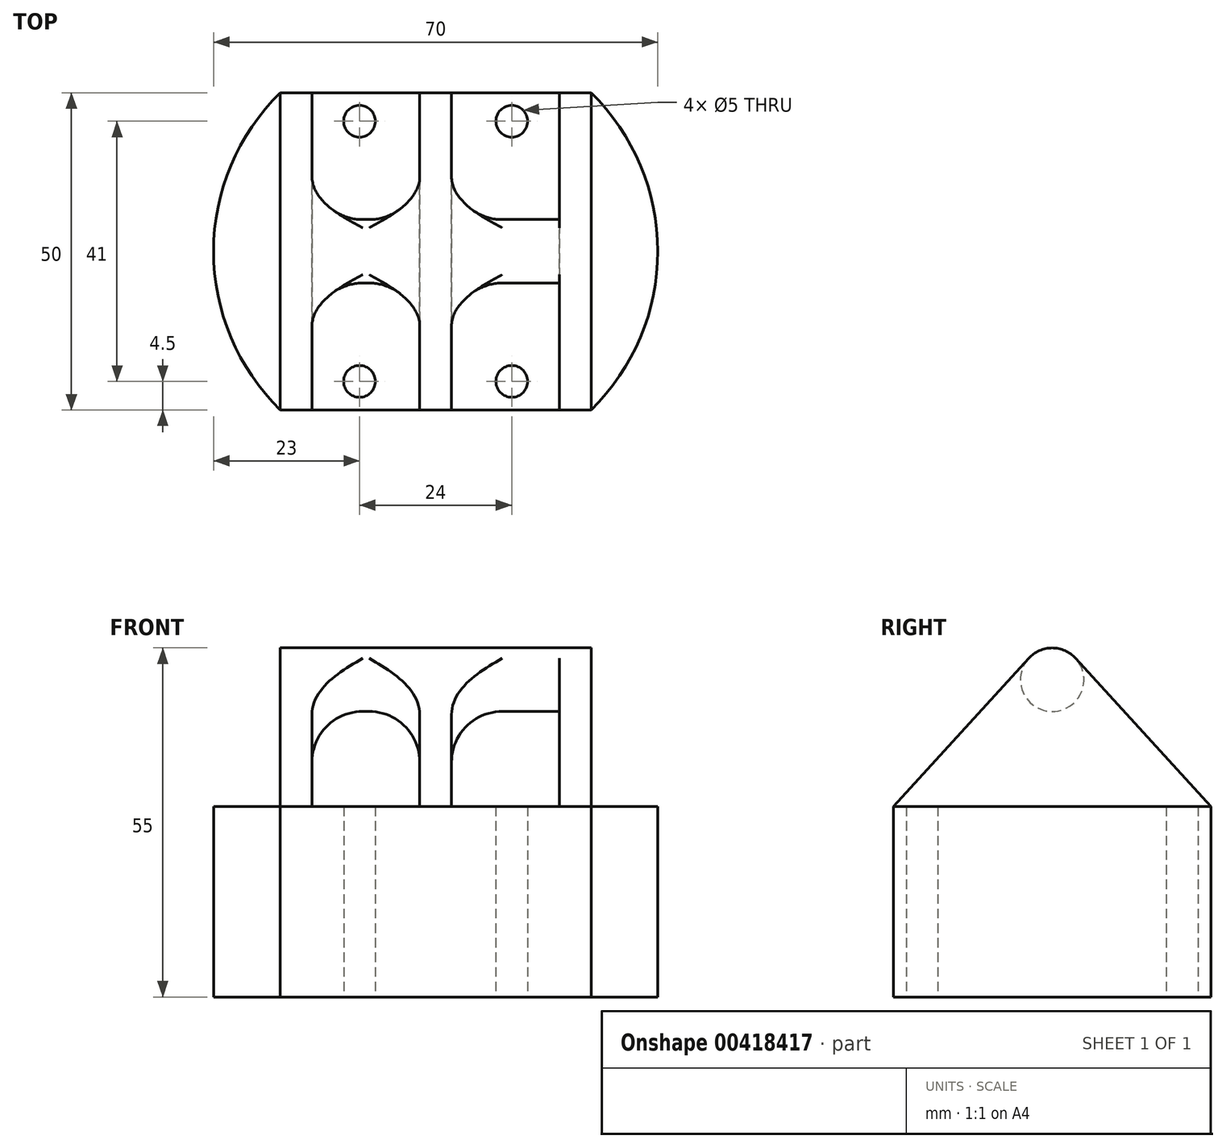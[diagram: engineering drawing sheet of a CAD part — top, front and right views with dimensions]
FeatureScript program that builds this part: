
annotation { "Feature Type Name" : "Feature", "Feature Type Description" : "" }
export const myFeature = defineFeature(function(context is Context, id is Id, definition is map)
    precondition{}
    {
        {
            var Q0;
            Q0=qCreatedBy(makeId("Top.planeOp"),FACE);
            var sketch = newSketch(context, id + "F0", { "sketchPlane" : qUnion([Q0])});
            skArc(sketch, "E0", {"start": v(-24.5, 25) * mm, "mid": v(-35, 0) * mm, "end": v(-24.5, -25) * mm});
            skLineSegment(sketch, "E1", {"start": v(-24.5, 25) * mm, "end": v(24.5, 25) * mm});
            skLineSegment(sketch, "E2", {"start": v(-24.5, -25) * mm, "end": v(24.5, -25) * mm});
            skArc(sketch, "E3.trimOffspring", {"start": v(24.5, -25) * mm, "mid": v(35, 0) * mm, "end": v(24.5, 25) * mm});
            skCircle(sketch, "E4", {"center": v(-12, -20.5) * mm, "radius": 2.5 * mm});
            skCircle(sketch, "E5", {"center": v(12, -20.5) * mm, "radius": 2.5 * mm});
            skCircle(sketch, "E6", {"center": v(12, 20.5) * mm, "radius": 2.5 * mm});
            skCircle(sketch, "E7", {"center": v(-12, 20.5) * mm, "radius": 2.5 * mm});
            skSolve(sketch);
        }
        {
            var Q0;
            Q0=qSketchRegion(id+"F0",true);
            extrude(context, id + "F1", {"entities" : qUnion([Q0]), "depth" : 5 * mm, "hasSecondDirection" : true, "secondDirectionOppositeDirection" : true, "secondDirectionDepth" : 25 * mm});
        }
        {
            var Q0;
            Q0=makeQuery(id+"F1.opExtrude","CAP_FACE",FACE,{"disambiguationData":[OSD([sQuery(id+"F0.wireOp",EDGE,"E0"),sQuery(id+"F0.wireOp",EDGE,"E1"),sQuery(id+"F0.wireOp",EDGE,"E2"),sQuery(id+"F0.wireOp",EDGE,"E3.trimOffspring")])],"isStart":false});
            var sketch = newSketch(context, id + "F2", { "sketchPlane" : qUnion([Q0])});
            skLineSegment(sketch, "E8.bottom", {"start": v(-24.5, 25) * mm, "end": v(-19.5, 25) * mm});
            skLineSegment(sketch, "E8.top", {"start": v(-24.5, -25) * mm, "end": v(-19.5, -25) * mm});
            skLineSegment(sketch, "E8.left", {"start": v(-24.5, 25) * mm, "end": v(-24.5, -25) * mm});
            skLineSegment(sketch, "E8.right", {"start": v(-19.5, 25) * mm, "end": v(-19.5, -25) * mm});
            skLineSegment(sketch, "E9.bottom", {"start": v(24.5, 25) * mm, "end": v(19.5, 25) * mm});
            skLineSegment(sketch, "E9.top", {"start": v(24.5, -25) * mm, "end": v(19.5, -25) * mm});
            skLineSegment(sketch, "E9.left", {"start": v(24.5, 25) * mm, "end": v(24.5, -25) * mm});
            skLineSegment(sketch, "E9.right", {"start": v(19.5, 25) * mm, "end": v(19.5, -25) * mm});
            skLineSegment(sketch, "E10.bottom", {"start": v(-2.5, 25) * mm, "end": v(2.5, 25) * mm});
            skLineSegment(sketch, "E10.top", {"start": v(-2.5, -25) * mm, "end": v(2.5, -25) * mm});
            skLineSegment(sketch, "E10.left", {"start": v(-2.5, 25) * mm, "end": v(-2.5, -25) * mm});
            skLineSegment(sketch, "E10.right", {"start": v(2.5, 25) * mm, "end": v(2.5, -25) * mm});
            skSolve(sketch);
        }
        {
            var Q0;
            Q0=qSketchRegion(id+"F2",true);
            extrude(context, id + "F3", {"entities" : qUnion([Q0]), "operationType" : NewBodyOperationType.ADD, "depth" : 25 * mm});
        }
        {
            var Q0;
            Q0=makeQuery(id+"F3.opExtrude","SWEPT_FACE",FACE,{"disambiguationData":[OSD([sQuery(id+"F2.wireOp",EDGE,"E8.left")])]});
            var sketch = newSketch(context, id + "F4", { "sketchPlane" : qUnion([Q0])});
            skArc(sketch, "E11", {"start": v(3.7, 28.37) * mm, "mid": v(0, 30) * mm, "end": v(-3.7, 28.37) * mm});
            skLineSegment(sketch, "E12", {"start": v(-25, 5) * mm, "end": v(-3.7, 28.37) * mm});
            skLineSegment(sketch, "E13", {"start": v(25, 5) * mm, "end": v(3.7, 28.37) * mm});
            skLineSegment(sketch, "E14", {"start": v(-25, 5) * mm, "end": v(-35, 5) * mm});
            skLineSegment(sketch, "E15", {"start": v(-35, 5) * mm, "end": v(-35, 40) * mm});
            skLineSegment(sketch, "E16", {"start": v(-35, 40) * mm, "end": v(35, 40) * mm});
            skLineSegment(sketch, "E17", {"start": v(35, 40) * mm, "end": v(35, 5) * mm});
            skLineSegment(sketch, "E18", {"start": v(35, 5) * mm, "end": v(25, 5) * mm});
            skSolve(sketch);
        }
        {
            var Q0;
            Q0=qSketchRegion(id+"F4",true);
            extrude(context, id + "F5", {"entities" : qUnion([Q0]), "operationType" : NewBodyOperationType.REMOVE, "endBound" : BoundingType.THROUGH_ALL, "oppositeDirection" : true, "depth" : 25 * mm});
        }
        {
            var Q0;
            Q0=makeQuery(id+"F3.opExtrude","SWEPT_FACE",FACE,{"disambiguationData":[OSD([sQuery(id+"F2.wireOp",EDGE,"E9.right")])]});
            var sketch = newSketch(context, id + "F6", { "sketchPlane" : qUnion([Q0])});
            skCircle(sketch, "E19", {"center": v(0, 25) * mm, "radius": 5 * mm});
            skSolve(sketch);
        }
        {
            var Q0;
            Q0=qSketchRegion(id+"F6",true);
            extrude(context, id + "F7", {"entities" : qUnion([Q0]), "operationType" : NewBodyOperationType.ADD, "depth" : 40 * mm});
        }
        {
            var Q0;
            Q0=makeQuery(id+"F7.boolean.opBoolean","INTERSECT",EDGE,{"derivedFrom":[makeQuery(id+"F3.opExtrude","SWEPT_FACE",FACE,{"disambiguationData":[OSD([sQuery(id+"F2.wireOp",EDGE,"E8.right")])]}),makeQuery(id+"F7.opExtrude","SWEPT_FACE",FACE,{"disambiguationData":[OSD([sQuery(id+"F6.wireOp",EDGE,"E19")])]})]});
            var Q1;
            Q1=makeQuery(id+"F7.boolean.opBoolean","INTERSECT",EDGE,{"derivedFrom":[makeQuery(id+"F3.opExtrude","SWEPT_FACE",FACE,{"disambiguationData":[OSD([sQuery(id+"F2.wireOp",EDGE,"E10.left")])]}),makeQuery(id+"F7.opExtrude","SWEPT_FACE",FACE,{"disambiguationData":[OSD([sQuery(id+"F6.wireOp",EDGE,"E19")])]})]});
            var Q2;
            Q2=makeQuery(id+"F7.boolean.opBoolean","INTERSECT",EDGE,{"derivedFrom":[makeQuery(id+"F3.opExtrude","SWEPT_FACE",FACE,{"disambiguationData":[OSD([sQuery(id+"F2.wireOp",EDGE,"E10.right")])]}),makeQuery(id+"F7.opExtrude","SWEPT_FACE",FACE,{"disambiguationData":[OSD([sQuery(id+"F6.wireOp",EDGE,"E19")])]})]});
            var Q3;
            Q3=makeQuery(id+"F7.opExtrude","CAP_EDGE",EDGE,{"disambiguationData":[OSD([sQuery(id+"F6.wireOp",EDGE,"E19")])],"isStart":true});
            fillet(context, id + "F8", {"entities" : qUnion([Q0, Q1, Q2, Q3]), "radius" : 8 * mm, "tangentPropagation" : true, "allowEdgeOverflow" : false});
        }
    });
